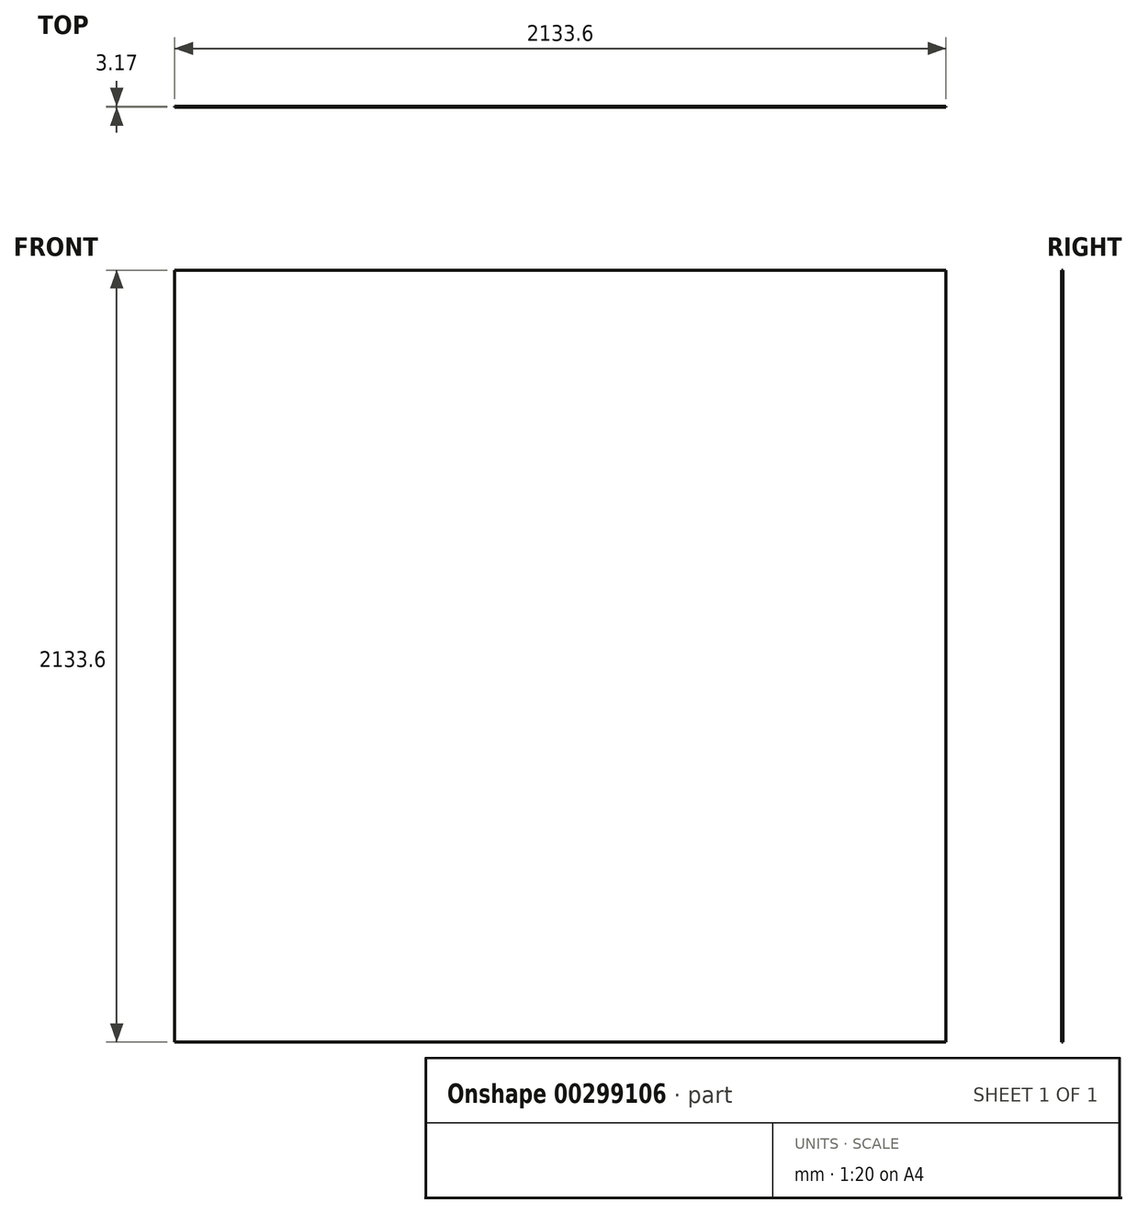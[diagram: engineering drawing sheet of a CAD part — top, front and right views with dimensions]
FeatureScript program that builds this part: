
annotation { "Feature Type Name" : "Feature", "Feature Type Description" : "" }
export const myFeature = defineFeature(function(context is Context, id is Id, definition is map)
    precondition{}
    {
        {
            var Q0;
            Q0=qCreatedBy(makeId("Front.planeOp"),FACE);
            var sketch = newSketch(context, id + "F0", { "sketchPlane" : qUnion([Q0])});
            skLineSegment(sketch, "E0.bottom", {"start": v(-1066.8, 1064.36) * mm, "end": v(1066.8, 1064.36) * mm});
            skLineSegment(sketch, "E0.top", {"start": v(-1066.8, -1069.24) * mm, "end": v(1066.8, -1069.24) * mm});
            skLineSegment(sketch, "E0.left", {"start": v(-1066.8, 1064.36) * mm, "end": v(-1066.8, -1069.24) * mm});
            skLineSegment(sketch, "E0.right", {"start": v(1066.8, 1064.36) * mm, "end": v(1066.8, -1069.24) * mm});
            skPoint(sketch, "E0.middle", {"position": v(0, -2.44) * mm});
            skSolve(sketch);
        }
        {
            var Q0;
            Q0 = qSketchRegion(id + "F0", true);
            extrude(context, id + "F1", {"entities" : qUnion([Q0]), "depth" : 3.17 * mm});
        }
        {
            var Q0;
            Q0=makeQuery(id+"F1.opExtrude","CAP_FACE",FACE,{"disambiguationData":[OSD([sQuery(id+"F0.wireOp",EDGE,"E0.bottom"),sQuery(id+"F0.wireOp",EDGE,"E0.top"),sQuery(id+"F0.wireOp",EDGE,"E0.left"),sQuery(id+"F0.wireOp",EDGE,"E0.right")])],"isStart":false});
            var sketch = newSketch(context, id + "F2", { "sketchPlane" : qUnion([Q0])});
            skLineSegment(sketch, "E1", {"start": v(-763.6, 1064.36) * mm, "end": v(-763.6, -1069.24) * mm, "construction": true});
            skSolve(sketch);
        }
        {
            var Q0;
            Q0=makeQuery(id+"F1.opExtrude","CAP_FACE",FACE,{"disambiguationData":[OSD([sQuery(id+"F0.wireOp",EDGE,"E0.bottom"),sQuery(id+"F0.wireOp",EDGE,"E0.top"),sQuery(id+"F0.wireOp",EDGE,"E0.left"),sQuery(id+"F0.wireOp",EDGE,"E0.right")])],"isStart":true});
            var sketch = newSketch(context, id + "F3", { "sketchPlane" : qUnion([Q0])});
            skLineSegment(sketch, "E2", {"start": v(1066.8, 761.16) * mm, "end": v(-1066.8, 761.16) * mm, "construction": true});
            skSolve(sketch);
        }
    });
